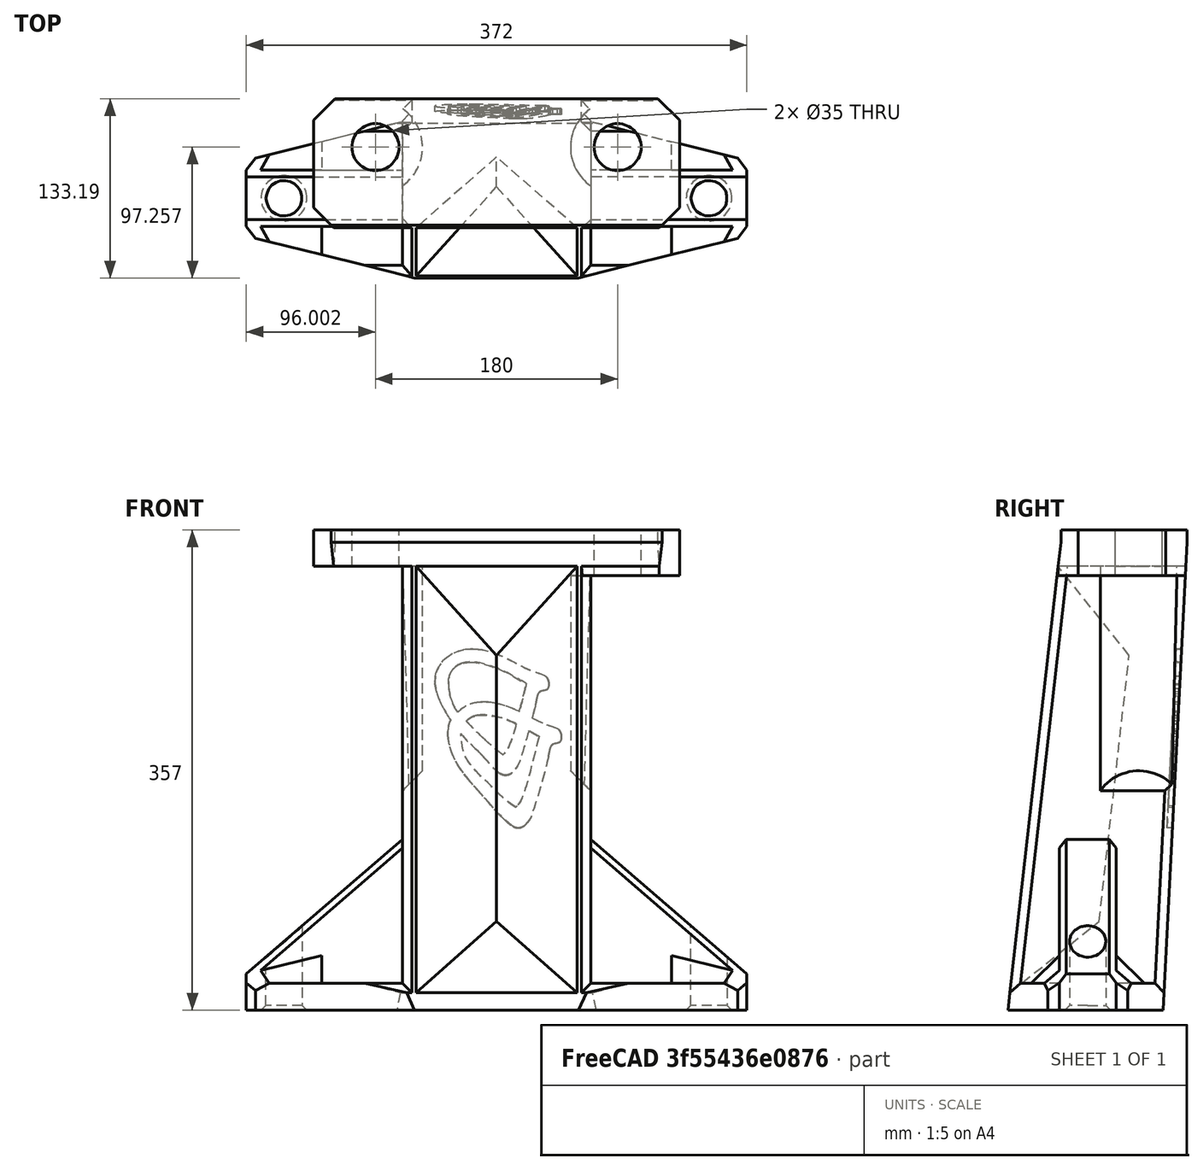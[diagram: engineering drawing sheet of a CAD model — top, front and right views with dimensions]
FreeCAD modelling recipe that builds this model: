
FCSTD DOCUMENT  (FreeCAD 1.0R39109 (Git))
Label: SE Carto Mount
License: All rights reserved
LicenseURL: https://en.wikipedia.org/wiki/All_rights_reserved
objects: Part::Feature×1, PartDesign::FeatureBase×1, Sketcher::SketchObject×1, PartDesign::Pad×1, PartDesign::Body×1
note: 9 computed .brp shape members not serialized (recipe doc carries the construction recipe); baked Part::Feature solids carry a one-line shape summary decoded from their .brp

FEATURE [Part::Feature] Part__Feature  label="(Unsaved)"
  shape: bbox 372.2 x 142.2 x 348.2 mm, 117 faces (baked)
FEATURE [PartDesign::FeatureBase] BaseFeature
  BaseFeature = -> Part__Feature
  Suppressed = false
FEATURE [Sketcher::SketchObject] Sketch
  ArcFitTolerance = 1e-06
  AttachmentSupport = -> [BaseFeature]
  ExternalGeometry = -> [BaseFeature]
  FullyConstrained = true
  MakeInternals = false
  MapMode = 5
  Placement = pos=(0,0,478) rot=(0,0,1;0rad)
  sketch-geometry (10):
    g0: LineSegment StartX=2313.59 StartY=421.836 StartZ=0 EndX=2553.73 EndY=421.836 EndZ=0
    g1: LineSegment StartX=2553.73 StartY=421.836 StartZ=0 EndX=2569.66 EndY=405.907 EndZ=0
    g2: LineSegment StartX=2569.66 StartY=405.907 StartZ=0 EndX=2569.66 EndY=340.907 EndZ=0
    g3: LineSegment StartX=2569.66 StartY=340.907 StartZ=0 EndX=2556.69 EndY=327.939 EndZ=0
    g4: LineSegment StartX=2556.69 StartY=327.939 StartZ=0 EndX=2310.63 EndY=327.939 EndZ=0
    g5: LineSegment StartX=2310.63 StartY=327.939 StartZ=0 EndX=2297.66 EndY=340.907 EndZ=0
    g6: LineSegment StartX=2297.66 StartY=340.907 StartZ=0 EndX=2297.66 EndY=405.907 EndZ=0
    g7: LineSegment StartX=2297.66 StartY=405.907 StartZ=0 EndX=2313.59 EndY=421.836 EndZ=0
    g8: Circle CenterX=2343.66 CenterY=385.907 CenterZ=0 NormalX=0 NormalY=0 NormalZ=1 AngleXU=0 Radius=17.5
    g9: Circle CenterX=2523.66 CenterY=385.907 CenterZ=0 NormalX=0 NormalY=0 NormalZ=1 AngleXU=0 Radius=17.5
  constraints (20):
    c: Coincident(g0,g-5)
    c: Coincident(g0,g-12)
    c: Coincident(g0,g1)
    c: Coincident(g1,g-11)
    c: Coincident(g1,g2)
    c: Coincident(g2,g-10)
    c: Coincident(g2,g3)
    c: Coincident(g3,g-9)
    c: Coincident(g3,g4)
    c: Coincident(g4,g-9)
    c: Coincident(g4,g5)
    c: Coincident(g5,g-7)
    c: Coincident(g5,g6)
    c: Coincident(g6,g-6)
    c: Coincident(g6,g7)
    c: Coincident(g7,g0)
    c: Coincident(g8,g-4)
    c: Equal(g8,g-4)
    c: Coincident(g9,g-3)
    c: Equal(g9,g-3)
FEATURE [PartDesign::Pad] Pad
  BaseFeature = -> BaseFeature
  Direction = (0,0,1)
  Length = 9
  Length2 = 10
  Profile = -> Sketch
  ReferenceAxis = -> Sketch [N_Axis]
  Refine = true
  Suppressed = false
  Type = 0
FEATURE [PartDesign::Body] Body
  AllowCompound = false
  BaseFeature = -> Part__Feature
  Group = -> [BaseFeature,Sketch,Pad]
  Origin = -> Origin
  Tip = -> Pad
